# Revit family: Vandal Resistant Exit_WM_Hosted_R16_V1.1
name_source: partatom
category: Lighting Fixtures
revit_build: Autodesk Revit 2016 (Build: 20150220_1215(x64)
units: mm (PartAtom-declared; Revit-internal decimal feet)

## family parameters
Always vertical = Yes
Cut with Voids When Loaded = No
Host = Wall
Light Source = Yes
OmniClass Number = 23.80.70.00
OmniClass Title = Lighting
Part Type = Normal
Room Calculation Point = No
Round Connector Dimension = Use Diameter
Shared = No

## types (4) — shared parameters
AS2293 Classification = C0=D3.2 C90=E8
Battery type = Lithium Nanophosphate, 3.3V 2500mAh
Charger Method = Intelligent Current Limited Constant Voltage
Color Filter = 16777215
Dimensions = 425 x 100 x 270mm (L x W x H)
Dimming Lamp Color Temperature Shift = <None>
Emit Shape Visible in Rendering = No
Emit from Rectangle Length = 1219 mm
Emit from Rectangle Width = 610 mm
IK Rating = IK10
IP Rating = IP20
Lamp = 6 x Duris E2 LED, 100,000hours
Mounting = Single Sided Wall Mount
Operating Mode = Maintained
Operating Temperature = 1C to 40C
Operating Voltage = 240V AC; 50Hz
Photometric Web File = ll19527_CVELED-CM-ZW.IES
Power Consumption = 1.4W (standby), 3.5W (max)
Tilt Angle = 0.00°
Viewing Distance = 24m

## per-type parameters (varying)
| type | Product Description | Testing Mode |
| LVELED-WM | L10 Optimum Cleverfit PRO Exit in Vandal Resistant Case, Wall Mounted, Enabled Clevertest Plus | Clevertest Plus Enabled (not activated by default) |
| LVELED-WM-CT | L10 Optimum Cleverfit PRO Exit in Vandal Resistant Case, Wall Mounted | Clevertest |
| LVELED-WM-DALI | L10 Optimum Cleverfit PRO Exit in Vandal Resistant Case, Wall Mounted | DALI Compatible |
| LVELED-WM-ZW | L10 Optimum Cleverfit PRO Exit in Vandal Resistant Case, Wall Mounted | Zoneworks Computerised Testing |

## geometry (parser evidence)
native form markers: Sweep x2
no freeform markers — native parametric forms only
